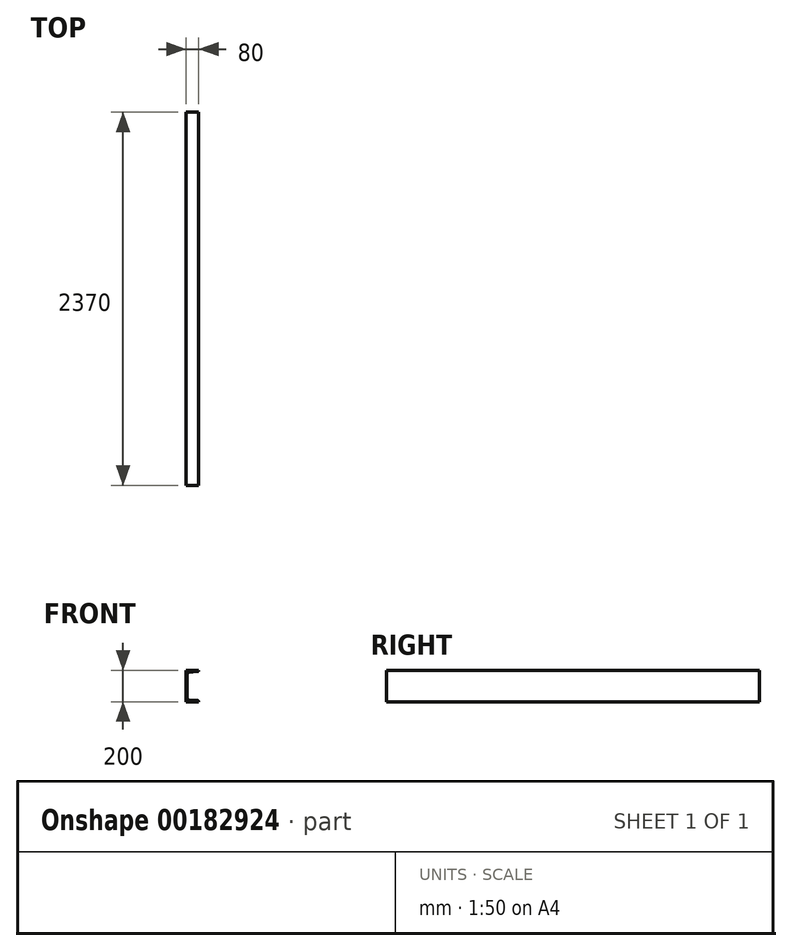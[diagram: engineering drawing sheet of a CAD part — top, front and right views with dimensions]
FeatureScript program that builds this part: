
annotation { "Feature Type Name" : "Feature", "Feature Type Description" : "" }
export const myFeature = defineFeature(function(context is Context, id is Id, definition is map)
    precondition{}
    {
        {
            var Q0;
            Q0=qCreatedBy(makeId("Front.planeOp"),FACE);
            var sketch = newSketch(context, id + "F0", { "sketchPlane" : qUnion([Q0])});
            skLineSegment(sketch, "E0.bottom", {"start": v(0, 0) * mm, "end": v(80, 0) * mm});
            skLineSegment(sketch, "E0.top", {"start": v(0, 100) * mm, "end": v(80, 100) * mm});
            skLineSegment(sketch, "E0.left", {"start": v(0, 0) * mm, "end": v(0, 100) * mm});
            skLineSegment(sketch, "E0.right", {"start": v(80, 98) * mm, "end": v(80, 100) * mm});
            skLineSegment(sketch, "E1.0", {"start": v(7.5, 0) * mm, "end": v(7.5, 75.16) * mm});
            skLineSegment(sketch, "E2", {"start": v(40, 100) * mm, "end": v(40, 89) * mm});
            skLineSegment(sketch, "E3.0", {"start": v(7.5, 89) * mm, "end": v(80, 89) * mm});
            skPoint(sketch, "E4.orphan", {"position": v(40, 0) * mm});
            skLineSegment(sketch, "E5", {"start": v(40, 89) * mm, "end": v(74.52, 92.02) * mm});
            skLineSegment(sketch, "E6", {"start": v(40, 89) * mm, "end": v(18.45, 87.11) * mm});
            skPoint(sketch, "E7.newPointB", {"position": v(80, 0) * mm});
            skArc(sketch, "E7.filletArc", {"start": v(74.52, 92.02) * mm, "mid": v(78.42, 93.94) * mm, "end": v(80, 98) * mm});
            skArc(sketch, "E8.filletArc", {"start": v(18.45, 87.11) * mm, "mid": v(10.65, 83.27) * mm, "end": v(7.5, 75.16) * mm});
            skLineSegment(sketch, "E9.MirrorCS", {"start": v(80, -98) * mm, "end": v(80, -100) * mm});
            skLineSegment(sketch, "E10.MirrorCS", {"start": v(40, -100) * mm, "end": v(40, -89) * mm});
            skArc(sketch, "E11.MirrorCS", {"start": v(74.52, -92.02) * mm, "mid": v(78.42, -93.94) * mm, "end": v(80, -98) * mm});
            skLineSegment(sketch, "E12.MirrorCS", {"start": v(0, -100) * mm, "end": v(80, -100) * mm});
            skLineSegment(sketch, "E13.MirrorCS", {"start": v(7.5, -89) * mm, "end": v(80, -89) * mm});
            skLineSegment(sketch, "E14.MirrorCS", {"start": v(40, -89) * mm, "end": v(74.52, -92.02) * mm});
            skLineSegment(sketch, "E15.MirrorCS", {"start": v(40, -89) * mm, "end": v(18.45, -87.11) * mm});
            skLineSegment(sketch, "E16.MirrorCS", {"start": v(0, 0) * mm, "end": v(0, -100) * mm});
            skArc(sketch, "E17.MirrorCS", {"start": v(18.45, -87.11) * mm, "mid": v(10.65, -83.27) * mm, "end": v(7.5, -75.16) * mm});
            skLineSegment(sketch, "E18.MirrorCS", {"start": v(7.5, 0) * mm, "end": v(7.5, -75.16) * mm});
            skSolve(sketch);
        }
        {
            var Q0;
            {var subQ1=sQuery(id+"F0.wireOp",EDGE,"E0.left");Q0=makeQuery(id+"F0.imprint","IMPRINT",FACE,{"disambiguationData":[TD([[makeQuery(id+"F0.imprint","IMPRINT",EDGE,{"derivedFrom":subQ1}),-1.0]])]});}
            var Q1;
            {var subQ1=sQuery(id+"F0.wireOp",EDGE,"E0.right");Q1=makeQuery(id+"F0.imprint","IMPRINT",FACE,{"disambiguationData":[TD([[makeQuery(id+"F0.imprint","IMPRINT",EDGE,{"derivedFrom":subQ1}),1.0]])]});}
            var Q2;
            {var subQ1=sQuery(id+"F0.wireOp",EDGE,"E10.MirrorCS");Q2=makeQuery(id+"F0.imprint","IMPRINT",FACE,{"disambiguationData":[TD([[makeQuery(id+"F0.imprint","IMPRINT",EDGE,{"derivedFrom":subQ1}),1.0]])]});}
            var Q3;
            {var subQ1=sQuery(id+"F0.wireOp",EDGE,"E9.MirrorCS");Q3=makeQuery(id+"F0.imprint","IMPRINT",FACE,{"disambiguationData":[TD([[makeQuery(id+"F0.imprint","IMPRINT",EDGE,{"derivedFrom":subQ1}),-1.0]])]});}
            extrude(context, id + "F1", {"entities" : qUnion([Q0, Q1, Q2, Q3]), "endBound" : BoundingType.SYMMETRIC, "depth" : 2370 * mm});
        }
    });
